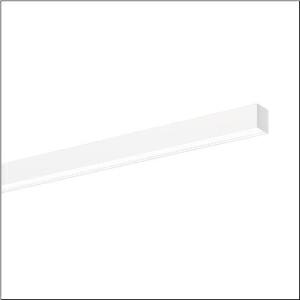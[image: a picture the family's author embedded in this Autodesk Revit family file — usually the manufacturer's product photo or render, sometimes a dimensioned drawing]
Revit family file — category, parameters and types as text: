
# Revit family: silica_21_51mx20tbt2w
name_source: partatom
category: Lighting Fixtures
units: mm (PartAtom-declared; Revit-internal decimal feet)

## family parameters
Cut with Voids When Loaded = No
Host = Face
Light Source = No
Part Type = Normal
Room Calculation Point = No
Round Connector Dimension = Use Diameter
Shared = No

## types (1)
- --- (1 x LED, 3000 lm, 25.6 W, 6500K)
    Apparent Load = 26 VA
    CIE Flux Codes = 48 79 96 100 100
    Color Rendering = 80
    Color Temperature = 6500K
    Default Elevation = 1800 mm
    Description = Silica 21, office luminaire, primary optical cover: cover, of PMMA, opal, light emission: direct distribution, primary light characteristic: symmetric, installation type: surface-mounted, LED, rated luminous flux: 3.000lm, luminous efficacy: 112lm/W, light colour: 8tw, colour temperature: 2700..6500K, control gear: DALI DT8, with terminal, 3+2-pole, max. 2.5mm², mains connection: 220..240V, AC, 50/60Hz, rated input power: 26.9W, luminaire housing, of aluminium, traffic white (RAL 9016), length: 1.504mm, width: 53mm, height: 53mm, protection rating (complete): IP20, insulation class (complete): insulation class I (protective earthing), certification: CE, permissible operating ambient temperature: 0..+35°C, standard: EN 50419, packaging unit: 1 piece
    Height = 53 mm
    Lamp = 1 x LED
    Lamp Light Flux = 3000 lm
    Lamp Power = 25.6 W
    Lamp count = 1
    Length = 1504 mm
    Luminous efficacy = 117 lm/W
    Manufacturer = Siteco
    ModVariant = No
    Model = 51MX20TBT2W
    Mounting Place = Ceiling
    Mounting Type = Surface mounted
    Number of Poles = 1
    OnlyDefault = Yes
    Power Factor = 1
    Product Name = Silica 21
    Product group = office luminaire | ceiling mounted
    ProductGroupID = 301
    Protection Class = Protection class I
    Protection Degree = IP 20
    RLX_Detail_Level = 1
    RLX_Emergency_Light_Flux = 0 lm
    RLX_Emergency_Type = 0
    RLX_Emergency_Type_DB = No
    RlxData = <blob elided: 20601 chars, md5=5999679e>
    Socket = socket
    Standby Power = 0 W
    System Light Flux = 3000 lm
    System Power = 26 W
    Type Comments = individual setting
    Type Image = l_1335877.jpg
    URL = http://relux.com
    VarID = @adj_140755
    Voltage = 0 V
    Weight = 0.00 kg
    Width = 53 mm

## geometry (parser evidence)
native form markers: Blend x4, Sweep x10
no freeform markers — native parametric forms only
